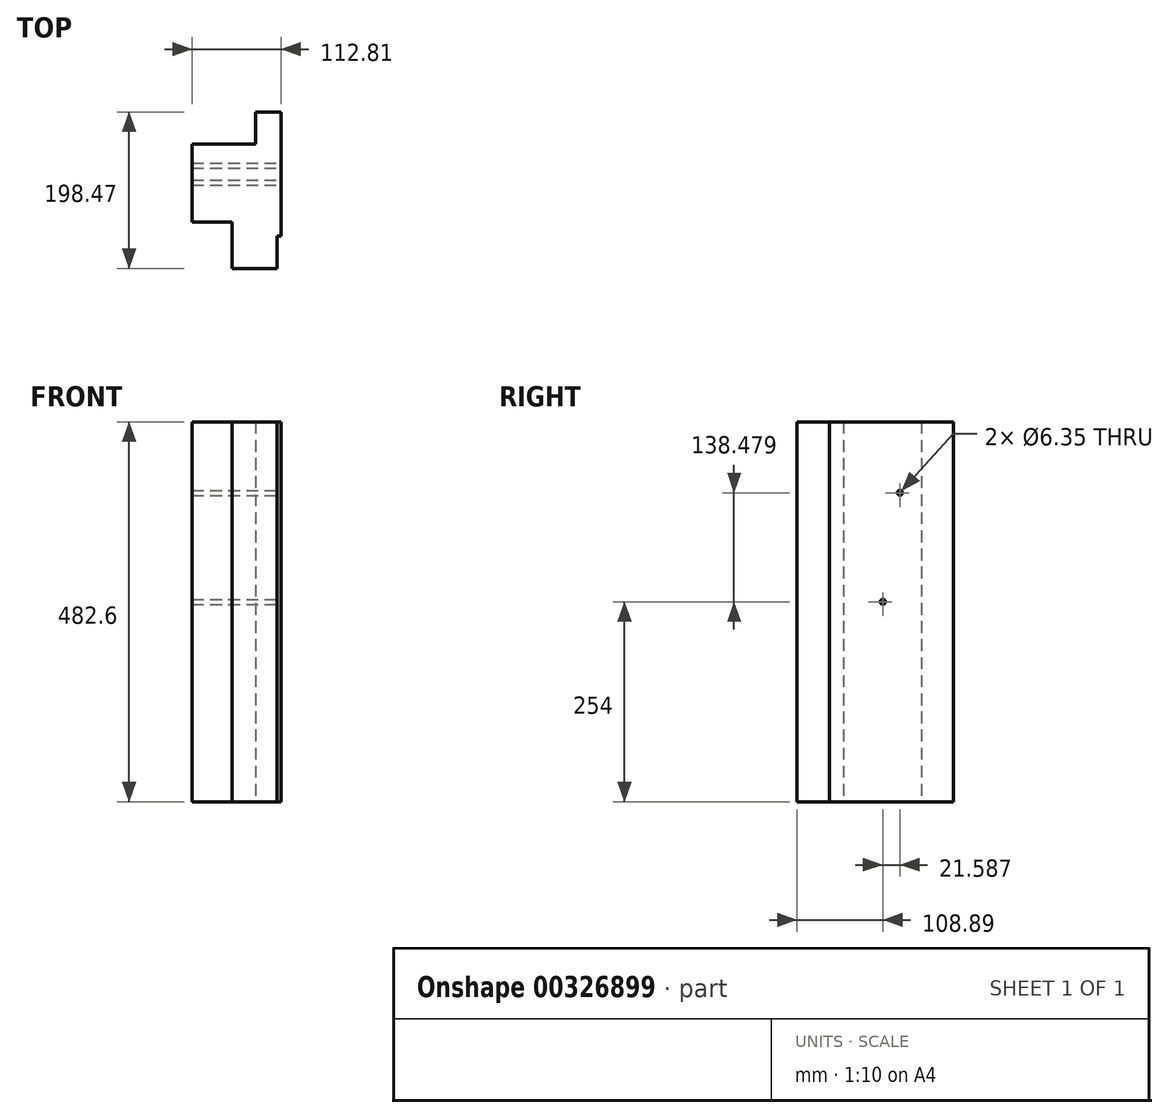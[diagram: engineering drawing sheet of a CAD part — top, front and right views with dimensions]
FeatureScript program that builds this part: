
annotation { "Feature Type Name" : "Feature", "Feature Type Description" : "" }
export const myFeature = defineFeature(function(context is Context, id is Id, definition is map)
    precondition{}
    {
        {
            var Q0;
            Q0=qCreatedBy(makeId("Top.planeOp"),FACE);
            var sketch = newSketch(context, id + "F0", { "sketchPlane" : qUnion([Q0])});
            skLineSegment(sketch, "E0.bottom", {"start": v(0, 0) * mm, "end": v(-51.04, 0) * mm});
            skLineSegment(sketch, "E0.top", {"start": v(29.53, 98.94) * mm, "end": v(-51.04, 98.94) * mm});
            skLineSegment(sketch, "E0.right", {"start": v(-51.04, 0) * mm, "end": v(-51.04, 98.94) * mm});
            skLineSegment(sketch, "E1.bottom", {"start": v(56.72, -17.61) * mm, "end": v(87.17, -17.61) * mm});
            skLineSegment(sketch, "E1.top", {"start": v(29.53, 139.74) * mm, "end": v(87.17, 139.74) * mm});
            skLineSegment(sketch, "E1.right", {"start": v(87.17, -17.61) * mm, "end": v(87.17, 139.74) * mm});
            skLineSegment(sketch, "E2.bottom", {"start": v(0, -58.73) * mm, "end": v(56.72, -58.73) * mm});
            skLineSegment(sketch, "E2.left", {"start": v(0, -58.73) * mm, "end": v(0, 0) * mm});
            skLineSegment(sketch, "E2.right", {"start": v(56.72, -58.73) * mm, "end": v(56.72, -17.61) * mm});
            skLineSegment(sketch, "E3.trimOffspring", {"start": v(29.53, 98.94) * mm, "end": v(29.53, 139.74) * mm});
            skPoint(sketch, "E4.orphan", {"position": v(29.53, -17.61) * mm});
            skPoint(sketch, "E0.left.start.orphan", {"position": v(29.53, 0) * mm});
            skSolve(sketch);
        }
        {
            var Q0;
            Q0=makeQuery(id+"F0.imprint","IMPRINT",FACE,{"disambiguationData":[TD([[makeQuery(id+"F0.imprint","IMPRINT",EDGE,{"derivedFrom":sQuery(id+"F0.wireOp",EDGE,"E0.bottom")}),-1.0]])]});
            extrude(context, id + "F1", {"entities" : qUnion([Q0]), "depth" : 254 * mm, "hasSecondDirection" : true, "secondDirectionOppositeDirection" : true, "secondDirectionDepth" : 254 * mm});
        }
        {
            var Q0;
            Q0=makeQuery(id+"F1.opExtrude","SWEPT_FACE",FACE,{"disambiguationData":[OSD([sQuery(id+"F0.wireOp",EDGE,"E1.right")])]});
            var sketch = newSketch(context, id + "F2", { "sketchPlane" : qUnion([Q0])});
            skCircle(sketch, "E5", {"center": v(71.75, 138.48) * mm, "radius": 33.24 * mm});
            skCircle(sketch, "E6", {"center": v(50.16, 0) * mm, "radius": 41.82 * mm});
            skSolve(sketch);
        }
        {
            var Q0;
            Q0=sQuery(id+"F2.wireOp",VERTEX,"E5.center");
            var Q1;
            Q1=sQuery(id+"F2.wireOp",VERTEX,"E6.center");
            var Q2;
            Q2=makeQuery(id+"F1.opExtrude","SWEPT_BODY",BODY,{"disambiguationData":[OSD([sQuery(id+"F0.wireOp",EDGE,"E0.bottom"),sQuery(id+"F0.wireOp",EDGE,"E0.top"),sQuery(id+"F0.wireOp",EDGE,"E0.right"),sQuery(id+"F0.wireOp",EDGE,"E1.bottom"),sQuery(id+"F0.wireOp",EDGE,"E1.top"),sQuery(id+"F0.wireOp",EDGE,"E1.right"),sQuery(id+"F0.wireOp",EDGE,"E2.bottom"),sQuery(id+"F0.wireOp",EDGE,"E2.left"),sQuery(id+"F0.wireOp",EDGE,"E2.right"),sQuery(id+"F0.wireOp",EDGE,"E3.trimOffspring")])]});
            hole(context, id + "F3", {"style" : HoleStyle.SIMPLE, "endStyle" : HoleEndStyle.THROUGH, "holeDiameter" : 6.35 * mm, "tappedDepth" : 12.7 * mm, "tapClearance" : 3, "locations" : qUnion([Q0, Q1]), "scope" : qUnion([Q2])});
        }
        {
            var Q0;
            Q0=makeQuery(id+"F1.opExtrude","SWEPT_FACE",FACE,{"disambiguationData":[OSD([sQuery(id+"F0.wireOp",EDGE,"E1.right")])]});
            var sketch = newSketch(context, id + "F4", { "sketchPlane" : qUnion([Q0])});
            skCircle(sketch, "E7", {"center": v(71.75, 138.48) * mm, "radius": 49.6 * mm});
            skCircle(sketch, "E8", {"center": v(54.16, -100.6) * mm, "radius": 48.83 * mm});
            skSolve(sketch);
        }
        {
            var Q0;
            Q0=makeQuery(id+"F4.imprint","IMPRINT",FACE,{"disambiguationData":[TD([[makeQuery(id+"F4.imprint","IMPRINT",EDGE,{"derivedFrom":sQuery(id+"F4.wireOp",EDGE,"E7")}),1.0]])]});
            extrude(context, id + "F5", {"entities" : qUnion([Q0]), "operationType" : NewBodyOperationType.REMOVE, "oppositeDirection" : true, "depth" : 25.4 * mm});
        }
        {
            var Q0;
            Q0=makeQuery(id+"F1.opExtrude","CAP_FACE",FACE,{"disambiguationData":[OSD([sQuery(id+"F0.wireOp",EDGE,"E0.bottom"),sQuery(id+"F0.wireOp",EDGE,"E0.top"),sQuery(id+"F0.wireOp",EDGE,"E0.right"),sQuery(id+"F0.wireOp",EDGE,"E1.bottom"),sQuery(id+"F0.wireOp",EDGE,"E1.top"),sQuery(id+"F0.wireOp",EDGE,"E1.right"),sQuery(id+"F0.wireOp",EDGE,"E2.bottom"),sQuery(id+"F0.wireOp",EDGE,"E2.left"),sQuery(id+"F0.wireOp",EDGE,"E2.right"),sQuery(id+"F0.wireOp",EDGE,"E3.trimOffspring")])],"isStart":false});
            extrude(context, id + "F6", {"entities" : qUnion([Q0]), "operationType" : NewBodyOperationType.REMOVE, "oppositeDirection" : true, "depth" : 25.4 * mm});
        }
        {
            var Q0;
            Q0=makeQuery(id+"F1.opExtrude","SWEPT_FACE",FACE,{"disambiguationData":[OSD([sQuery(id+"F0.wireOp",EDGE,"E1.right")])]});
            extrude(context, id + "F7", {"entities" : qUnion([Q0]), "operationType" : NewBodyOperationType.REMOVE, "oppositeDirection" : true, "depth" : 25.4 * mm});
        }
    });
